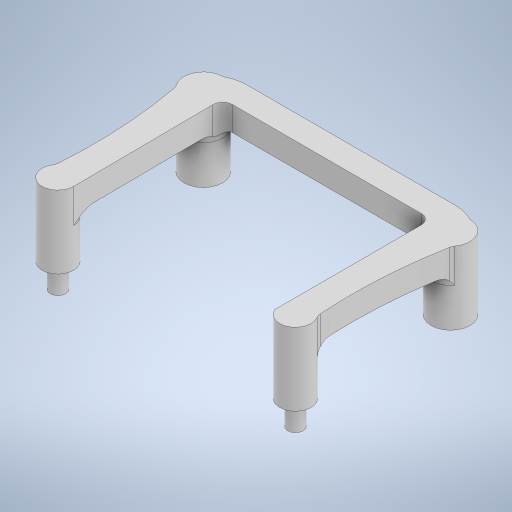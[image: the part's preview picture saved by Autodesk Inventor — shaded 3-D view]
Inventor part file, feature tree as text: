
AUTODESK INVENTOR PART (.ipt)
format: ipt  version: 2024.2 (Build 282272000, 272)  size: 399,360 bytes
history: native  units: mm
features: extrude x4, sketch x4, fillet x1, projected_geometry x1
ambient origin geometry x8: Origin, YZ Plane, XZ Plane, XY Plane, X Axis, Y Axis, Z Axis, Center Point
bodies: Solid1 (feature_tree)
feature tree (10):
  extrude  "Extrusion1"  Depth=5.0mm TaperAngle=0.0deg
  extrude  "Extrusion2"  Depth=5.2mm
  extrude  "Extrusion3"  Depth=8.0mm
  extrude  "Extrusion4"  Depth=2.0mm
  fillet  "Fillet1"  Radius=51.0mm
  sketch  "Sketch2"  dims[d0=6.5mm d1=5.0mm d2=0.0mm]
  sketch  "Sketch3"  dims[d3=6.5mm d4=5.2mm]
  sketch  "Sketch4"  dims[d5=5.2mm d6=8.0mm]
  projected_geometry  "Projected Loop1"
  sketch  "Sketch5"  dims[d7=8.0mm d8=49.0mm d9=51.0mm d11=31.0mm d12=3.2mm d13=3.2mm d14=5.0mm d15=0.0mm d16=3.0mm d17=3.0mm d18=5.0mm d19=0.0mm d21=1.0mm d24=100.0mm d25=100.0mm d26=2.5mm d27=3.0mm d28=3.0mm d29=2.5mm d30=5.0mm d31=0.0mm d32=5.0mm d33=4.0mm d34=4.0mm d35=2.0mm d20=0.5mm]
